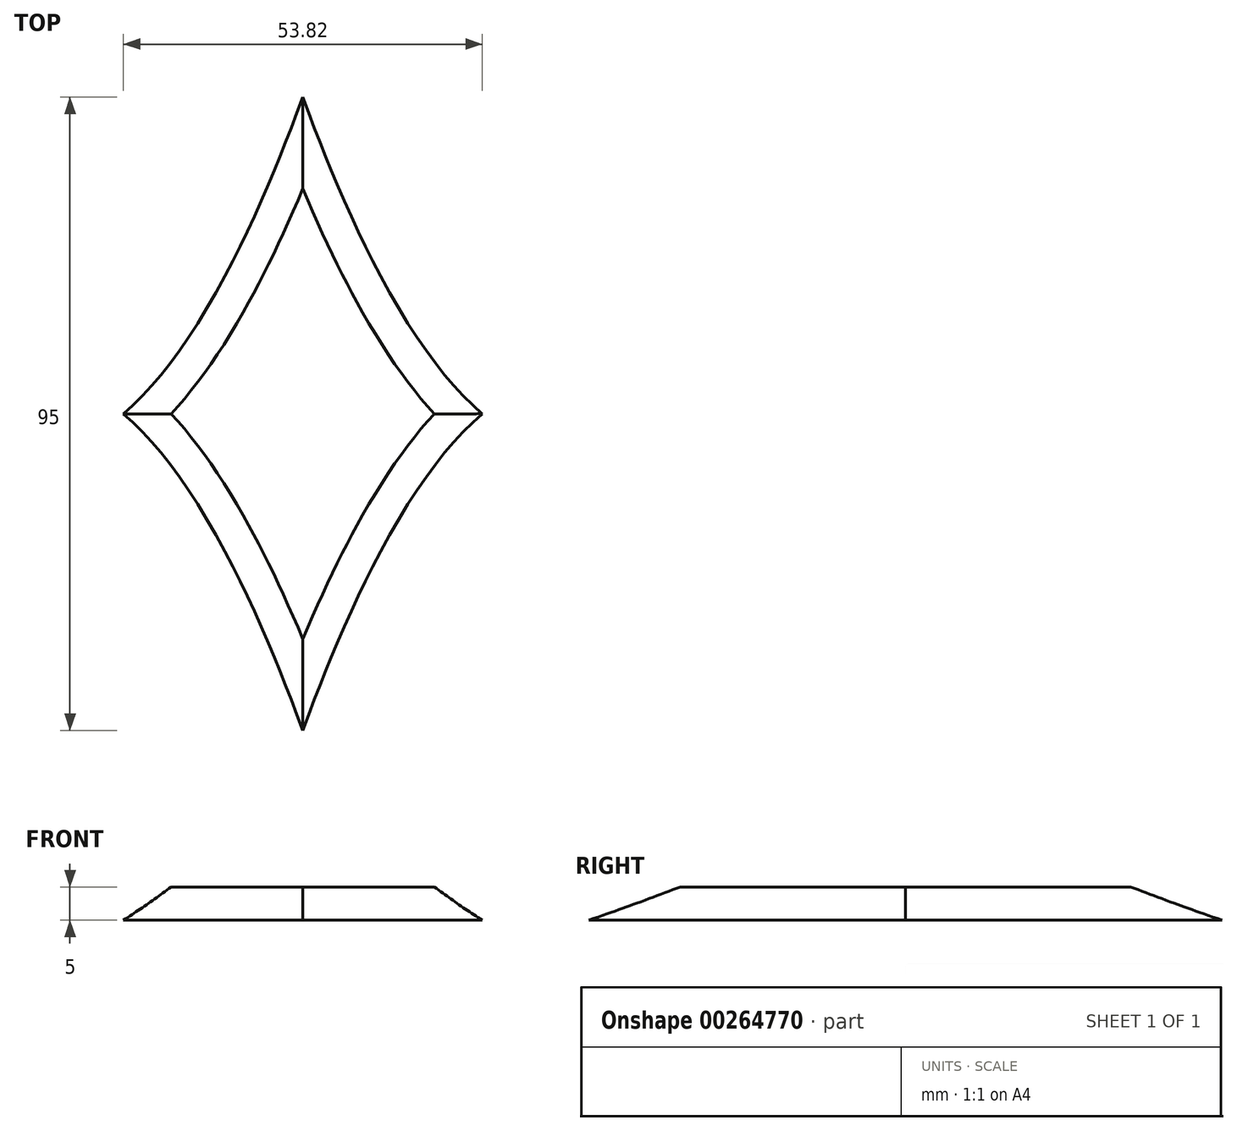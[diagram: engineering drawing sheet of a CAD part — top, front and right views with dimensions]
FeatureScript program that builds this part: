
annotation { "Feature Type Name" : "Feature", "Feature Type Description" : "" }
export const myFeature = defineFeature(function(context is Context, id is Id, definition is map)
    precondition{}
    {
        {
            var Q0;
            Q0=qCreatedBy(makeId("Top.planeOp"),FACE);
            var sketch = newSketch(context, id + "F0", { "sketchPlane" : qUnion([Q0])});
            skLineSegment(sketch, "E0", {"start": v(0, 55.19) * mm, "end": v(0, -54.81) * mm, "construction": true});
            skSolve(sketch);
        }
        {
            var Q0;
            Q0=qCreatedBy(makeId("Top.planeOp"),FACE);
            cPlane(context, id + "F1", {"entities" : qUnion([Q0]), "cplaneType" : CPlaneType.OFFSET, "offset" : 15 * mm, "width" : 150 * mm, "height" : 150 * mm});
        }
        {
            var Q0;
            Q0=qCreatedBy(makeId("Top.planeOp"),FACE);
            var sketch = newSketch(context, id + "F2", { "sketchPlane" : qUnion([Q0])});
            skFitSpline(sketch, "E1", {"points": [v(0, 47.5) * mm, v(-26.9, 0) * mm], "startDerivative": vector(-17.02, -46) * mm, "endDerivative": vector(-36.6, -31.48) * mm});
            skFitSpline(sketch, "E2.MirrorCS", {"points": [v(0, -47.5) * mm, v(-26.9, 0) * mm], "startDerivative": vector(-17.02, 46) * mm, "endDerivative": vector(-36.6, 31.48) * mm});
            skFitSpline(sketch, "E3.MirrorCS", {"points": [v(0, 47.5) * mm, v(26.9, 0) * mm], "startDerivative": vector(17.02, -46) * mm, "endDerivative": vector(36.6, -31.48) * mm});
            skFitSpline(sketch, "E4.MirrorCS", {"points": [v(0, -47.5) * mm, v(26.9, 0) * mm], "startDerivative": vector(17.02, 46) * mm, "endDerivative": vector(36.6, 31.48) * mm});
            skLineSegment(sketch, "E5", {"start": v(0, 47.5) * mm, "end": v(0, -47.5) * mm, "construction": true});
            skSolve(sketch);
        }
        {
            var Q0;
            Q0=makeQuery(id+"F2.imprint","IMPRINT",FACE,{"disambiguationData":[TD([[makeQuery(id+"F2.imprint","IMPRINT",EDGE,{"derivedFrom":sQuery(id+"F2.wireOp",EDGE,"E1")}),1.0]])]});
            extrude(context, id + "F3", {"entities" : qUnion([Q0]), "depth" : 10 * mm, "offsetDistance" : 25 * mm});
        }
        {
            var Q0;
            Q0=makeQuery(id+"F3.opExtrude","CAP_EDGE",EDGE,{"disambiguationData":[OSD([sQuery(id+"F2.wireOp",EDGE,"E1")])],"isStart":false});
            var Q1;
            Q1=makeQuery(id+"F3.opExtrude","CAP_EDGE",EDGE,{"disambiguationData":[OSD([sQuery(id+"F2.wireOp",EDGE,"E2.MirrorCS")])],"isStart":false});
            var Q2;
            Q2=makeQuery(id+"F3.opExtrude","CAP_EDGE",EDGE,{"disambiguationData":[OSD([sQuery(id+"F2.wireOp",EDGE,"E4.MirrorCS")])],"isStart":false});
            var Q3;
            Q3=makeQuery(id+"F3.opExtrude","CAP_EDGE",EDGE,{"disambiguationData":[OSD([sQuery(id+"F2.wireOp",EDGE,"E3.MirrorCS")])],"isStart":false});
            chamfer(context, id + "F4", {"entities" : qUnion([Q0, Q1, Q2, Q3]), "width" : 5 * mm, "tangentPropagation" : true});
        }
        {
            var Q0;
            Q0=makeQuery(id+"F3.opExtrude","CAP_FACE",FACE,{"disambiguationData":[OSD([sQuery(id+"F2.wireOp",EDGE,"E1"),sQuery(id+"F2.wireOp",EDGE,"E2.MirrorCS"),sQuery(id+"F2.wireOp",EDGE,"E3.MirrorCS"),sQuery(id+"F2.wireOp",EDGE,"E4.MirrorCS")])],"isStart":true});
            extrude(context, id + "F5", {"entities" : qUnion([Q0]), "operationType" : NewBodyOperationType.REMOVE, "oppositeDirection" : true, "depth" : 5 * mm, "offsetDistance" : 25 * mm});
        }
    });
